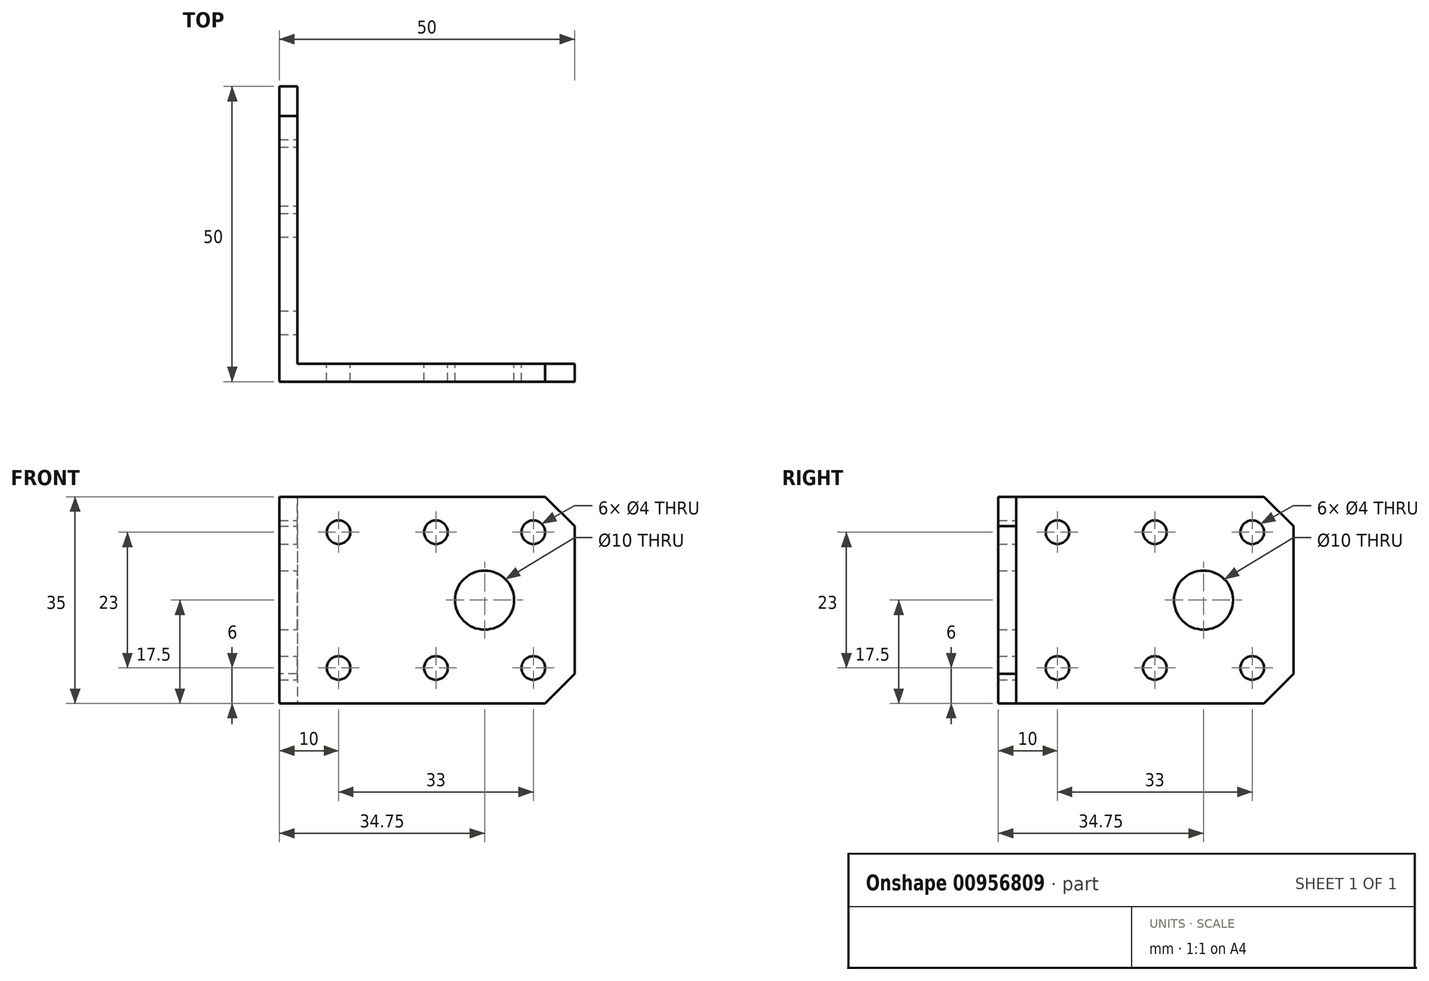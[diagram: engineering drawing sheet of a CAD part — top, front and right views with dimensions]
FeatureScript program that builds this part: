
annotation { "Feature Type Name" : "Feature", "Feature Type Description" : "" }
export const myFeature = defineFeature(function(context is Context, id is Id, definition is map)
    precondition{}
    {
        {
            var Q0;
            Q0=qCreatedBy(makeId("Top.planeOp"),FACE);
            var sketch = newSketch(context, id + "F0", { "sketchPlane" : qUnion([Q0])});
            skLineSegment(sketch, "E0", {"start": v(0, 0) * mm, "end": v(50, 0) * mm});
            skLineSegment(sketch, "E1", {"start": v(50, 0) * mm, "end": v(50, 3) * mm});
            skLineSegment(sketch, "E2", {"start": v(50, 3) * mm, "end": v(3, 3) * mm});
            skLineSegment(sketch, "E3", {"start": v(3, 3) * mm, "end": v(3, 50) * mm});
            skLineSegment(sketch, "E4", {"start": v(3, 50) * mm, "end": v(0, 50) * mm});
            skLineSegment(sketch, "E5", {"start": v(0, 50) * mm, "end": v(0, 0) * mm});
            skSolve(sketch);
        }
        {
            var Q0;
            Q0 = qSketchRegion(id + "F0", true);
            extrude(context, id + "F1", {"entities" : qUnion([Q0]), "depth" : 35 * mm, "offsetDistance" : 25 * mm});
        }
        {
            var Q0;
            Q0=makeQuery(id+"F1.opExtrude","SWEPT_FACE",FACE,{"disambiguationData":[OSD([sQuery(id+"F0.wireOp",EDGE,"E2")])]});
            var sketch = newSketch(context, id + "F2", { "sketchPlane" : qUnion([Q0])});
            skCircle(sketch, "E6", {"center": v(-34.75, 17.5) * mm, "radius": 5 * mm});
            skLineSegment(sketch, "E7", {"start": v(-50, 17.5) * mm, "end": v(-3, 17.5) * mm, "construction": true});
            skCircle(sketch, "E8", {"center": v(-43, 29) * mm, "radius": 2 * mm});
            skCircle(sketch, "E9", {"center": v(-26.5, 29) * mm, "radius": 2 * mm});
            skCircle(sketch, "E10", {"center": v(-10, 29) * mm, "radius": 2 * mm});
            skCircle(sketch, "E11", {"center": v(-43, 6) * mm, "radius": 2 * mm});
            skCircle(sketch, "E12", {"center": v(-26.5, 6) * mm, "radius": 2 * mm});
            skCircle(sketch, "E13", {"center": v(-10, 6) * mm, "radius": 2 * mm});
            skLineSegment(sketch, "E14", {"start": v(-43, 29) * mm, "end": v(-26.5, 29) * mm, "construction": true});
            skLineSegment(sketch, "E15", {"start": v(-26.5, 29) * mm, "end": v(-10, 29) * mm, "construction": true});
            skLineSegment(sketch, "E16", {"start": v(-43, 6) * mm, "end": v(-26.5, 6) * mm, "construction": true});
            skLineSegment(sketch, "E17", {"start": v(-26.5, 6) * mm, "end": v(-10, 6) * mm, "construction": true});
            skLineSegment(sketch, "E18", {"start": v(-26.5, 35) * mm, "end": v(-26.5, 0) * mm, "construction": true});
            skLineSegment(sketch, "E19", {"start": v(-34.75, 29) * mm, "end": v(-34.75, 6) * mm, "construction": true});
            skSolve(sketch);
        }
        {
            var Q0;
            Q0 = qSketchRegion(id + "F2", true);
            extrude(context, id + "F3", {"entities" : qUnion([Q0]), "operationType" : NewBodyOperationType.REMOVE, "endBound" : BoundingType.UP_TO_NEXT, "oppositeDirection" : true, "depth" : 25 * mm, "offsetDistance" : 25 * mm});
        }
        {
            var Q0;
            Q0=makeQuery(id+"F1.opExtrude","SWEPT_FACE",FACE,{"disambiguationData":[OSD([sQuery(id+"F0.wireOp",EDGE,"E3")])]});
            var sketch = newSketch(context, id + "F4", { "sketchPlane" : qUnion([Q0])});
            skCircle(sketch, "E20", {"center": v(34.75, 17.5) * mm, "radius": 5 * mm});
            skLineSegment(sketch, "E21", {"start": v(50, 17.5) * mm, "end": v(3, 17.5) * mm, "construction": true});
            skLineSegment(sketch, "E22", {"start": v(10, 29) * mm, "end": v(26.5, 29) * mm, "construction": true});
            skLineSegment(sketch, "E23", {"start": v(26.5, 29) * mm, "end": v(43, 29) * mm, "construction": true});
            skLineSegment(sketch, "E24", {"start": v(10, 6) * mm, "end": v(26.5, 6) * mm, "construction": true});
            skLineSegment(sketch, "E25", {"start": v(26.5, 6) * mm, "end": v(43, 6) * mm, "construction": true});
            skCircle(sketch, "E26", {"center": v(10, 29) * mm, "radius": 2 * mm});
            skCircle(sketch, "E27", {"center": v(26.5, 29) * mm, "radius": 2 * mm});
            skCircle(sketch, "E28", {"center": v(43, 29) * mm, "radius": 2 * mm});
            skCircle(sketch, "E29", {"center": v(10, 6) * mm, "radius": 2 * mm});
            skCircle(sketch, "E30", {"center": v(26.5, 6) * mm, "radius": 2 * mm});
            skCircle(sketch, "E31", {"center": v(43, 6) * mm, "radius": 2 * mm});
            skLineSegment(sketch, "E32", {"start": v(26.5, 35) * mm, "end": v(26.5, 0) * mm, "construction": true});
            skLineSegment(sketch, "E33", {"start": v(34.75, 29) * mm, "end": v(34.75, 6) * mm, "construction": true});
            skSolve(sketch);
        }
        {
            var Q0;
            Q0 = qSketchRegion(id + "F4", true);
            extrude(context, id + "F5", {"entities" : qUnion([Q0]), "operationType" : NewBodyOperationType.REMOVE, "endBound" : BoundingType.UP_TO_NEXT, "oppositeDirection" : true, "depth" : 25 * mm, "offsetDistance" : 25 * mm});
        }
        {
            var Q0;
            Q0=makeQuery(id+"F1.opExtrude","CAP_EDGE",EDGE,{"disambiguationData":[OSD([sQuery(id+"F0.wireOp",EDGE,"E1")])],"isStart":false});
            var Q1;
            Q1=makeQuery(id+"F1.opExtrude","CAP_EDGE",EDGE,{"disambiguationData":[OSD([sQuery(id+"F0.wireOp",EDGE,"E1")])],"isStart":true});
            chamfer(context, id + "F6", {"entities" : qUnion([Q0, Q1]), "width" : 5 * mm, "tangentPropagation" : true});
        }
        {
            var Q0;
            Q0=makeQuery(id+"F1.opExtrude","CAP_EDGE",EDGE,{"disambiguationData":[OSD([sQuery(id+"F0.wireOp",EDGE,"E4")])],"isStart":false});
            var Q1;
            Q1=makeQuery(id+"F1.opExtrude","CAP_EDGE",EDGE,{"disambiguationData":[OSD([sQuery(id+"F0.wireOp",EDGE,"E4")])],"isStart":true});
            chamfer(context, id + "F7", {"entities" : qUnion([Q0, Q1]), "width" : 5 * mm, "tangentPropagation" : true});
        }
    });
